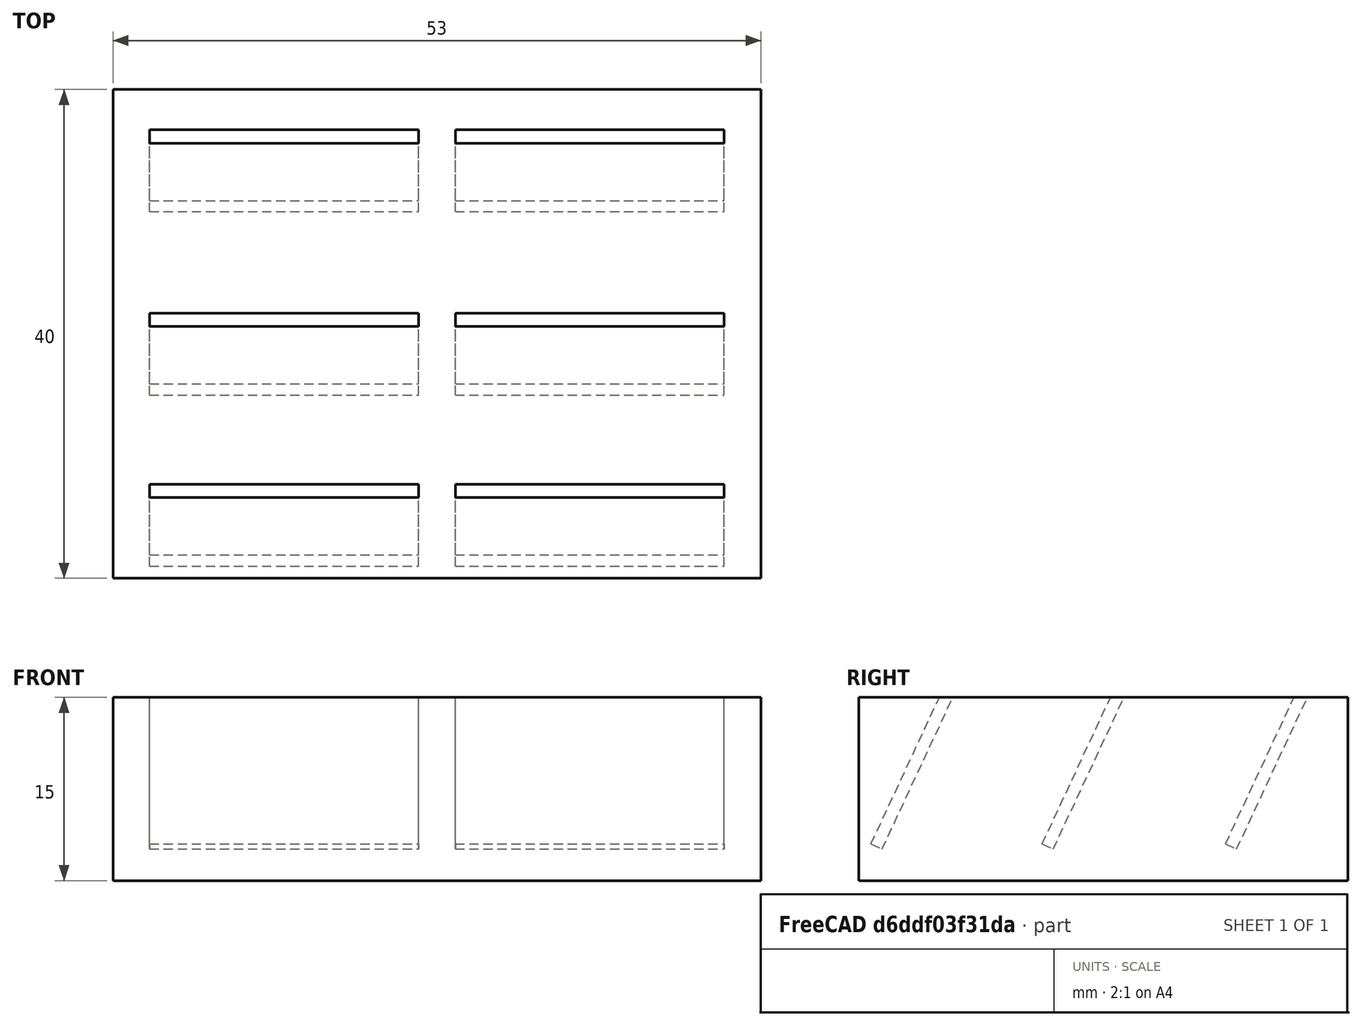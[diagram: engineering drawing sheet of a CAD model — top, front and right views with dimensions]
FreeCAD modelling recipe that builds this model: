
FCSTD DOCUMENT  (FreeCAD 1.0R39109 (Git))
Label: Dual-M.2-Drive-Holder
License: All rights reserved
LicenseURL: https://en.wikipedia.org/wiki/All_rights_reserved
objects: Part::Box×7, Part::MultiFuse×1, Part::Cut×1
note: 9 computed .brp shape members not serialized (recipe doc carries the construction recipe); baked Part::Feature solids carry a one-line shape summary decoded from their .brp

FEATURE [Part::Box] Box  label="Cube"
  AttacherType = Attacher::AttachEngine3D
  Height = 15
  Length = 53
  Width = 40
FEATURE [Part::Box] Box001  label="Cube001"
  AttacherType = Attacher::AttachEngine3D
  Height = 15
  Length = 22
  Placement = pos=(3,15,3) rot=(1,0,0;-0.436332rad)
  Width = 1
FEATURE [Part::Box] Box002  label="Cube002"
  AttacherType = Attacher::AttachEngine3D
  Height = 15
  Length = 22
  Placement = pos=(28,15,3) rot=(1,0,0;-0.436332rad)
  Width = 1
FEATURE [Part::Box] Box003  label="Cube003"
  AttacherType = Attacher::AttachEngine3D
  Height = 15
  Length = 22
  Placement = pos=(3,30,3) rot=(1,0,0;-0.436332rad)
  Width = 1
FEATURE [Part::Box] Box004  label="Cube004"
  AttacherType = Attacher::AttachEngine3D
  Height = 15
  Length = 22
  Placement = pos=(28,30,3) rot=(1,0,0;-0.436332rad)
  Width = 1
FEATURE [Part::Box] Box005  label="Cube005"
  AttacherType = Attacher::AttachEngine3D
  Height = 15
  Length = 22
  Placement = pos=(3,1,3) rot=(1,0,0;-0.436332rad)
  Width = 1
FEATURE [Part::Box] Box006  label="Cube006"
  AttacherType = Attacher::AttachEngine3D
  Height = 15
  Length = 22
  Placement = pos=(28,1,3) rot=(1,0,0;-0.436332rad)
  Width = 1
FEATURE [Part::MultiFuse] Fusion
  Shapes = -> [Box005,Box001,Box003,Box006,Box002,Box004]
FEATURE [Part::Cut] Cut
  Base = -> Box
  Tool = -> Fusion
